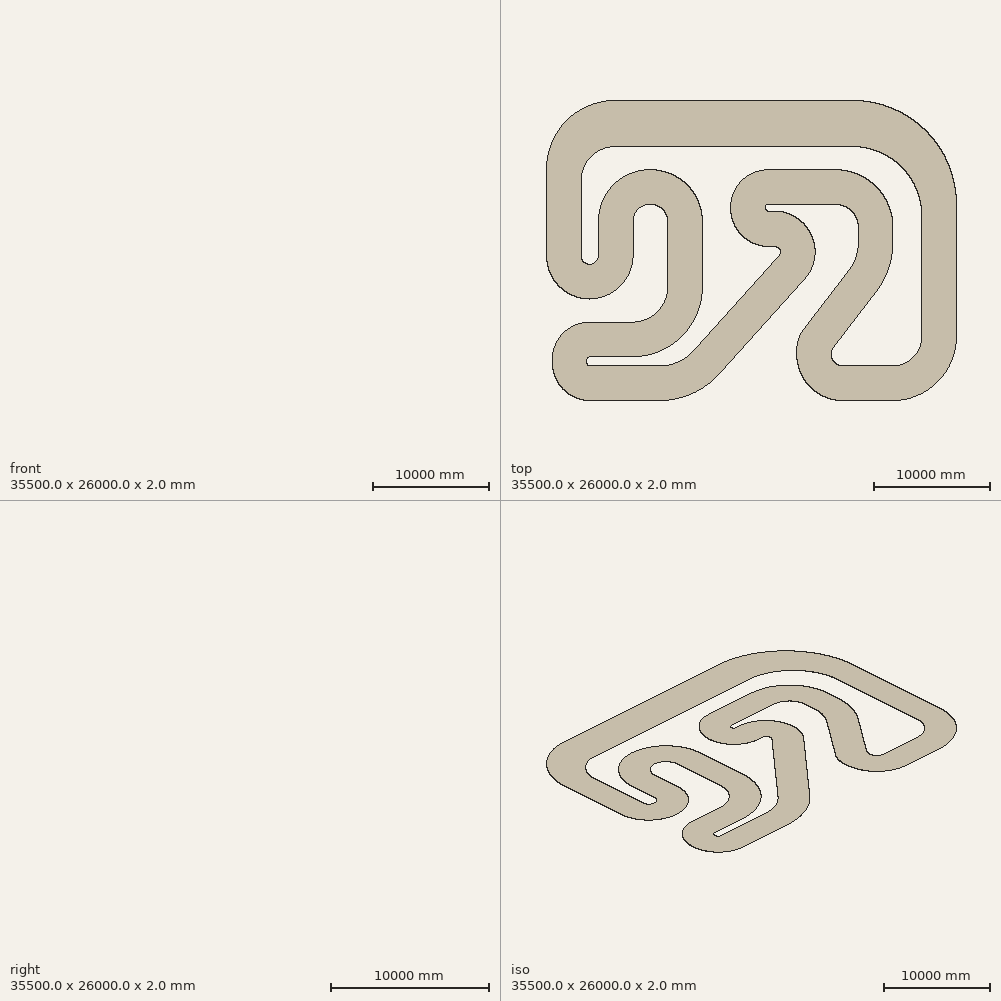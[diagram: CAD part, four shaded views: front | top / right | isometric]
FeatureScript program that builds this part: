
annotation { "Feature Type Name" : "Feature", "Feature Type Description" : "" }
export const myFeature = defineFeature(function(context is Context, id is Id, definition is map)
    precondition{}
    {
        {
            var Q0;
            Q0=qCreatedBy(makeId("Top.planeOp"),FACE);
            var sketch = newSketch(context, id + "F0", { "sketchPlane" : qUnion([Q0])});
            skLineSegment(sketch, "E0.bottom", {"start": v(-22176.77, 19518.87) * mm, "end": v(14823.23, 19518.87) * mm});
            skLineSegment(sketch, "E0.top", {"start": v(-22176.77, -9481.13) * mm, "end": v(14823.23, -9481.13) * mm});
            skLineSegment(sketch, "E0.left", {"start": v(-22176.77, 19518.87) * mm, "end": v(-22176.77, -9481.13) * mm});
            skLineSegment(sketch, "E0.right", {"start": v(14823.23, 19518.87) * mm, "end": v(14823.23, -9481.13) * mm});
            skLineSegment(sketch, "E1.bottom", {"start": v(-15676.77, 18518.87) * mm, "end": v(4823.23, 18518.87) * mm});
            skLineSegment(sketch, "E1.top", {"start": v(3991.9, -7481.13) * mm, "end": v(8323.23, -7481.13) * mm});
            skLineSegment(sketch, "E1.right", {"start": v(13823.23, 9518.87) * mm, "end": v(13823.23, -1981.13) * mm});
            skLineSegment(sketch, "E2", {"start": v(-15676.77, 14518.87) * mm, "end": v(4823.23, 14518.87) * mm});
            skLineSegment(sketch, "E3", {"start": v(10823.23, 8518.87) * mm, "end": v(10823.23, -1981.13) * mm});
            skArc(sketch, "E4.filletArc", {"start": v(10823.23, 8518.87) * mm, "mid": v(9065.87, 12761.5) * mm, "end": v(4823.23, 14518.87) * mm});
            skLineSegment(sketch, "E5", {"start": v(8323.23, 6181.02) * mm, "end": v(8323.23, 7518.87) * mm});
            skLineSegment(sketch, "E6", {"start": v(3323.23, 12518.87) * mm, "end": v(-2414.5, 12518.87) * mm});
            skLineSegment(sketch, "E7", {"start": v(8323.23, -4481.13) * mm, "end": v(3991.9, -4481.13) * mm});
            skLineSegment(sketch, "E8", {"start": v(3198.63, -2872.26) * mm, "end": v(6876.1, 1918.89) * mm});
            skLineSegment(sketch, "E9", {"start": v(612.1, -1314.97) * mm, "end": v(4496.3, 3745.52) * mm});
            skLineSegment(sketch, "E10", {"start": v(5323.23, 7518.87) * mm, "end": v(5323.23, 6181.02) * mm});
            skLineSegment(sketch, "E11", {"start": v(3323.23, 9518.87) * mm, "end": v(-2414.5, 9518.87) * mm});
            skLineSegment(sketch, "E12", {"start": v(-8.1, -3141.6) * mm, "end": v(-8.1, -3481.13) * mm});
            skLineSegment(sketch, "E13", {"start": v(1585.5, 5361.12) * mm, "end": v(1585.5, 5361.12) * mm});
            skLineSegment(sketch, "E14", {"start": v(687.74, 3020.53) * mm, "end": v(-6672.28, -5162.3) * mm});
            skLineSegment(sketch, "E15", {"start": v(-2414.5, 5861.12) * mm, "end": v(-1914.5, 5861.12) * mm});
            skLineSegment(sketch, "E16", {"start": v(-1542.75, 5026.75) * mm, "end": v(-8902.77, -3156.08) * mm});
            skLineSegment(sketch, "E17", {"start": v(-11876.77, -4481.13) * mm, "end": v(-17876.77, -4481.13) * mm});
            skArc(sketch, "E18.filletArc", {"start": v(8323.23, 7518.87) * mm, "mid": v(6858.77, 11054.4) * mm, "end": v(3323.23, 12518.87) * mm});
            skArc(sketch, "E19.filletArc", {"start": v(8323.23, -7481.13) * mm, "mid": v(12212.32, -5870.22) * mm, "end": v(13823.23, -1981.13) * mm});
            skArc(sketch, "E20.filletArc", {"start": v(-8.1, -3481.13) * mm, "mid": v(1163.47, -6309.56) * mm, "end": v(3991.9, -7481.13) * mm});
            skLineSegment(sketch, "E21", {"start": v(-11876.77, -7481.13) * mm, "end": v(-17876.77, -7481.13) * mm});
            skLineSegment(sketch, "E22", {"start": v(-21676.77, 12518.87) * mm, "end": v(-21676.77, 5068.87) * mm});
            skArc(sketch, "E23.filletArc", {"start": v(-15676.77, 18518.87) * mm, "mid": v(-19919.4, 16761.5) * mm, "end": v(-21676.77, 12518.87) * mm});
            skArc(sketch, "E24.filletArc", {"start": v(13823.23, 9518.87) * mm, "mid": v(11187.2, 15882.83) * mm, "end": v(4823.23, 18518.87) * mm});
            skArc(sketch, "E25.filletArc", {"start": v(3198.63, -2872.26) * mm, "mid": v(3094.99, -3923.36) * mm, "end": v(3991.9, -4481.13) * mm});
            skArc(sketch, "E26.filletArc", {"start": v(8323.23, -4481.13) * mm, "mid": v(10091, -3748.9) * mm, "end": v(10823.23, -1981.13) * mm});
            skPoint(sketch, "E27.visualSharp", {"position": v(-16929.36, 30181.47) * mm});
            skArc(sketch, "E28.filletArc", {"start": v(4496.3, 3745.52) * mm, "mid": v(5110.86, 4894.99) * mm, "end": v(5323.23, 6181.02) * mm});
            skArc(sketch, "E29.filletArc", {"start": v(5323.23, 7518.87) * mm, "mid": v(4737.45, 8933.08) * mm, "end": v(3323.23, 9518.87) * mm});
            skArc(sketch, "E30.filletArc", {"start": v(687.74, 3020.53) * mm, "mid": v(1353.36, 4107.7) * mm, "end": v(1585.5, 5361.12) * mm});
            skArc(sketch, "E31.filletArc", {"start": v(1585.5, 5361.12) * mm, "mid": v(714.84, 7707.87) * mm, "end": v(-1475.78, 8918.87) * mm});
            skArc(sketch, "E32.filletArc", {"start": v(-1542.75, 5026.75) * mm, "mid": v(-1457.78, 5564.6) * mm, "end": v(-1914.5, 5861.12) * mm});
            skArc(sketch, "E33.filletArc", {"start": v(-11876.77, -7481.13) * mm, "mid": v(-9027.92, -6875.2) * mm, "end": v(-6672.28, -5162.3) * mm});
            skArc(sketch, "E34.filletArc", {"start": v(6876.1, 1918.89) * mm, "mid": v(7951.58, 3930.46) * mm, "end": v(8323.23, 6181.02) * mm});
            skArc(sketch, "E35.filletArc", {"start": v(612.1, -1314.97) * mm, "mid": v(151.17, -2177.07) * mm, "end": v(-8.1, -3141.6) * mm});
            skLineSegment(sketch, "E36", {"start": v(-18176.77, -4181.13) * mm, "end": v(-18176.77, -3981.13) * mm});
            skLineSegment(sketch, "E37", {"start": v(-17876.77, -3681.13) * mm, "end": v(-14176.77, -3681.13) * mm});
            skLineSegment(sketch, "E38", {"start": v(-21176.77, -4181.13) * mm, "end": v(-21176.77, -3981.13) * mm});
            skLineSegment(sketch, "E39", {"start": v(-17876.77, -681.13) * mm, "end": v(-14176.77, -681.13) * mm});
            skLineSegment(sketch, "E40", {"start": v(-11176.77, 2318.87) * mm, "end": v(-11176.77, 8018.87) * mm});
            skLineSegment(sketch, "E41", {"start": v(-8176.77, 2318.87) * mm, "end": v(-8176.77, 8018.87) * mm});
            skLineSegment(sketch, "E42", {"start": v(-17176.77, 8018.87) * mm, "end": v(-17176.77, 5068.87) * mm});
            skLineSegment(sketch, "E43", {"start": v(-18676.77, 11518.87) * mm, "end": v(-18676.77, 5068.87) * mm});
            skArc(sketch, "E44.filletArc", {"start": v(-14176.77, -681.13) * mm, "mid": v(-12055.45, 197.55) * mm, "end": v(-11176.77, 2318.87) * mm});
            skArc(sketch, "E45.filletArc", {"start": v(-14176.77, -3681.13) * mm, "mid": v(-9934.13, -1923.77) * mm, "end": v(-8176.77, 2318.87) * mm});
            skArc(sketch, "E46.filletArc", {"start": v(-17876.77, -681.13) * mm, "mid": v(-20210.22, -1647.68) * mm, "end": v(-21176.77, -3981.13) * mm});
            skArc(sketch, "E47.filletArc", {"start": v(-21176.77, -4181.13) * mm, "mid": v(-20210.22, -6514.58) * mm, "end": v(-17876.77, -7481.13) * mm});
            skPoint(sketch, "E48.visualSharp", {"position": v(-18176.77, -6375.29) * mm});
            skArc(sketch, "E48.filletArc", {"start": v(-18176.77, -4181.13) * mm, "mid": v(-18088.9, -4393.26) * mm, "end": v(-17876.77, -4481.13) * mm});
            skPoint(sketch, "E49.visualSharp", {"position": v(-18176.77, -3681.13) * mm});
            skArc(sketch, "E49.filletArc", {"start": v(-17876.77, -3681.13) * mm, "mid": v(-18088.9, -3769) * mm, "end": v(-18176.77, -3981.13) * mm});
            skArc(sketch, "E50.filletArc", {"start": v(-15676.77, 14518.87) * mm, "mid": v(-17798.09, 13640.19) * mm, "end": v(-18676.77, 11518.87) * mm});
            skArc(sketch, "E51.filletArc", {"start": v(-11876.77, -4481.13) * mm, "mid": v(-10248.86, -4134.88) * mm, "end": v(-8902.77, -3156.08) * mm});
            skLineSegment(sketch, "E52", {"start": v(-14176.77, 8018.87) * mm, "end": v(-14176.77, 5068.87) * mm});
            skArc(sketch, "E53", {"start": v(-17176.77, 8018.87) * mm, "mid": v(-12676.77, 12518.87) * mm, "end": v(-8176.77, 8018.87) * mm});
            skArc(sketch, "E54", {"start": v(-14176.77, 8018.87) * mm, "mid": v(-12676.77, 9518.87) * mm, "end": v(-11176.77, 8018.87) * mm});
            skLineSegment(sketch, "E55", {"start": v(-1475.78, 8918.87) * mm, "end": v(-2414.5, 8918.87) * mm});
            skArc(sketch, "E56", {"start": v(-2414.5, 9518.87) * mm, "mid": v(-2714.5, 9218.87) * mm, "end": v(-2414.5, 8918.87) * mm});
            skArc(sketch, "E57", {"start": v(-21676.77, 5068.87) * mm, "mid": v(-17926.77, 1318.87) * mm, "end": v(-14176.77, 5068.87) * mm});
            skArc(sketch, "E58", {"start": v(-18676.77, 5068.87) * mm, "mid": v(-17926.77, 4318.87) * mm, "end": v(-17176.77, 5068.87) * mm});
            skArc(sketch, "E59", {"start": v(-2414.5, 12518.87) * mm, "mid": v(-5743.38, 9190) * mm, "end": v(-2414.5, 5861.12) * mm});
            skLineSegment(sketch, "E60", {"start": v(-7841.96, 17551.42) * mm, "end": v(1625.19, 17551.42) * mm});
            skLineSegment(sketch, "E61", {"start": v(1625.19, 17551.42) * mm, "end": v(3865.5, 17009.4) * mm});
            skLineSegment(sketch, "E62", {"start": v(3865.5, 17009.4) * mm, "end": v(8599.08, 13757.33) * mm});
            skLineSegment(sketch, "E63", {"start": v(8599.08, 13757.33) * mm, "end": v(11020.07, 10975) * mm});
            skLineSegment(sketch, "E64", {"start": v(11020.07, 10975) * mm, "end": v(13260.4, 7108.64) * mm});
            skLineSegment(sketch, "E65", {"start": v(13260.4, 7108.64) * mm, "end": v(13260.4, -479.54) * mm});
            skLineSegment(sketch, "E66", {"start": v(13260.4, -479.54) * mm, "end": v(11634.35, -2792.12) * mm});
            skLineSegment(sketch, "E67", {"start": v(11634.35, -2792.12) * mm, "end": v(7334.39, -6261) * mm});
            skLineSegment(sketch, "E68", {"start": v(7334.39, -6261) * mm, "end": v(4299.12, -5899.66) * mm});
            skLineSegment(sketch, "E69", {"start": v(4299.12, -5899.66) * mm, "end": v(2807.08, -3734.04) * mm});
            skLineSegment(sketch, "E70", {"start": v(2807.08, -3734.04) * mm, "end": v(3106.69, -1527.43) * mm});
            skLineSegment(sketch, "E71", {"start": v(3106.69, -1527.43) * mm, "end": v(5599.95, 5410.33) * mm});
            skLineSegment(sketch, "E72", {"start": v(5599.95, 5410.33) * mm, "end": v(5599.95, 7840.77) * mm});
            skLineSegment(sketch, "E73", {"start": v(5599.95, 7840.77) * mm, "end": v(4487.2, 9618.3) * mm});
            skLineSegment(sketch, "E74", {"start": v(4487.2, 9618.3) * mm, "end": v(1858.89, 11593.33) * mm});
            skLineSegment(sketch, "E75", {"start": v(1858.89, 11593.33) * mm, "end": v(-1544.25, 11593.33) * mm});
            skLineSegment(sketch, "E76", {"start": v(-1544.25, 11593.33) * mm, "end": v(-2592.53, 10377.92) * mm});
            skLineSegment(sketch, "E77", {"start": v(-2592.53, 10377.92) * mm, "end": v(-2896.38, 8630.78) * mm});
            skLineSegment(sketch, "E78", {"start": v(-2896.38, 8630.78) * mm, "end": v(-1544.25, 6321.51) * mm});
            skLineSegment(sketch, "E79", {"start": v(-1544.25, 6321.51) * mm, "end": v(-875.77, 4118.6) * mm});
            skLineSegment(sketch, "E80", {"start": v(-875.77, 4118.6) * mm, "end": v(-1316.36, 1702.98) * mm});
            skLineSegment(sketch, "E81", {"start": v(-1316.36, 1702.98) * mm, "end": v(-2000.02, 624.3) * mm});
            skLineSegment(sketch, "E82", {"start": v(-2000.02, 624.3) * mm, "end": v(-9482.7, -4248.3) * mm});
            skLineSegment(sketch, "E83", {"start": v(-9482.7, -4248.3) * mm, "end": v(-13402.37, -6041.02) * mm});
            skLineSegment(sketch, "E84", {"start": v(-13402.37, -6041.02) * mm, "end": v(-17205.41, -6381.2) * mm});
            skLineSegment(sketch, "E85", {"start": v(-17205.41, -6381.2) * mm, "end": v(-18174.05, -5669.65) * mm});
            skLineSegment(sketch, "E86", {"start": v(-18174.05, -5669.65) * mm, "end": v(-18335.19, -4165.67) * mm});
            skLineSegment(sketch, "E87", {"start": v(-18335.19, -4165.67) * mm, "end": v(-17873.25, -3037.68) * mm});
            skLineSegment(sketch, "E88", {"start": v(-17873.25, -3037.68) * mm, "end": v(-13715.8, -899.87) * mm});
            skLineSegment(sketch, "E89", {"start": v(-13715.8, -899.87) * mm, "end": v(-11396.84, 311.13) * mm});
            skLineSegment(sketch, "E90", {"start": v(-11396.84, 311.13) * mm, "end": v(-8818.57, 3942.18) * mm});
            skLineSegment(sketch, "E91", {"start": v(-8818.57, 3942.18) * mm, "end": v(-8818.57, 7874.03) * mm});
            skLineSegment(sketch, "E92", {"start": v(-8818.57, 7874.03) * mm, "end": v(-9871.37, 9356.53) * mm});
            skLineSegment(sketch, "E93", {"start": v(-9871.37, 9356.53) * mm, "end": v(-12449.63, 9850.7) * mm});
            skLineSegment(sketch, "E94", {"start": v(-12449.63, 9850.7) * mm, "end": v(-14082.52, 9292.07) * mm});
            skLineSegment(sketch, "E95", {"start": v(-14082.52, 9292.07) * mm, "end": v(-14705.6, 7336.9) * mm});
            skLineSegment(sketch, "E96", {"start": v(-14705.6, 7336.9) * mm, "end": v(-17515.46, 4212.9) * mm});
            skLineSegment(sketch, "E97", {"start": v(-17515.46, 4212.9) * mm, "end": v(-18205.37, 3936.45) * mm});
            skLineSegment(sketch, "E98", {"start": v(-18205.37, 3936.45) * mm, "end": v(-19215.23, 4844.77) * mm});
            skLineSegment(sketch, "E99", {"start": v(-19215.23, 4844.77) * mm, "end": v(-20564.35, 8456.68) * mm});
            skLineSegment(sketch, "E100", {"start": v(-20564.35, 8456.68) * mm, "end": v(-20356.3, 11505.08) * mm});
            skLineSegment(sketch, "E101", {"start": v(-20356.3, 11505.08) * mm, "end": v(-18161.62, 13945.1) * mm});
            skLineSegment(sketch, "E102", {"start": v(-18161.62, 13945.1) * mm, "end": v(-12207.48, 17411.6) * mm});
            skLineSegment(sketch, "E103", {"start": v(-11439.8, 17521.02) * mm, "end": v(-7841.96, 17551.42) * mm});
            skSolve(sketch);
        }
        {
            var Q0;
            Q0=makeQuery(id+"F0.imprint","IMPRINT",FACE,{"disambiguationData":[TD([[makeQuery(id+"F0.imprint","IMPRINT",EDGE,{"derivedFrom":sQuery(id+"F0.wireOp",EDGE,"E1.bottom")}),-1.0]])]});
            extrude(context, id + "F1", {"entities" : qUnion([Q0]), "depth" : 2 * mm, "offsetDistance" : 25 * mm});
        }
    });
